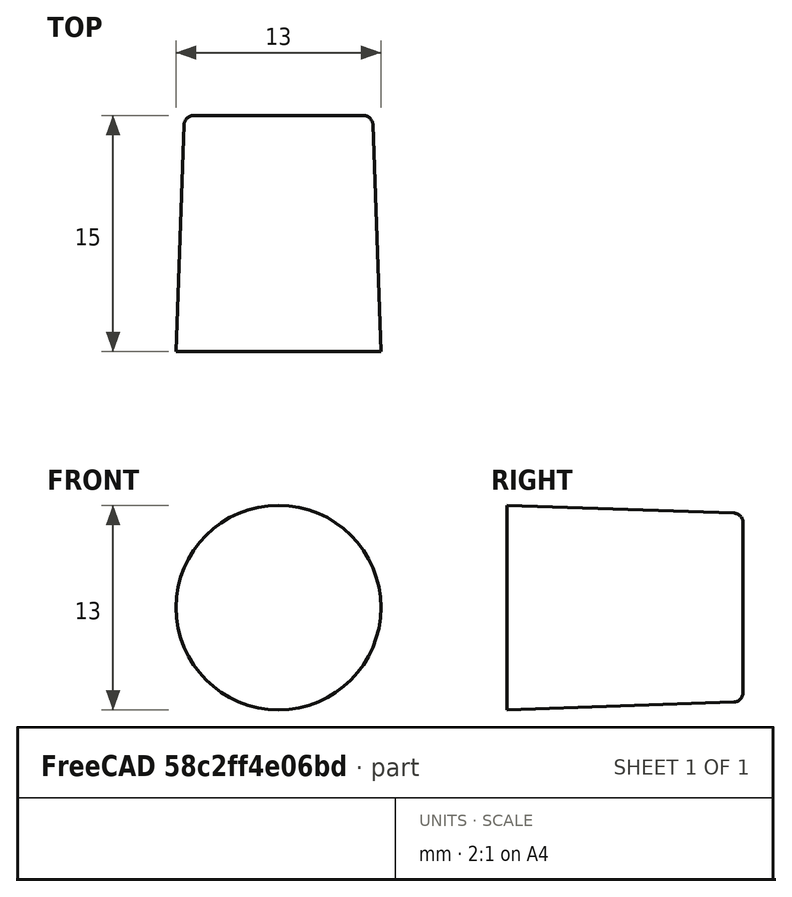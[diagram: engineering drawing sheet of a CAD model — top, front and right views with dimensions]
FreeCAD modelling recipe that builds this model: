
FCSTD DOCUMENT  (FreeCAD 0.18R15619 (Git))
Label: knob-rubber
License: All rights reserved
LicenseURL: http://en.wikipedia.org/wiki/All_rights_reserved
objects: Sketcher::SketchObject×1, PartDesign::Revolution×1, PartDesign::Body×1
note: 4 computed .brp shape members not serialized (recipe doc carries the construction recipe); baked Part::Feature solids carry a one-line shape summary decoded from their .brp

FEATURE [Sketcher::SketchObject] Sketch
  MapMode = 5
  Support = -> [XY_Plane]
  sketch-geometry (5):
    g0: LineSegment StartX=0 StartY=0 StartZ=0 EndX=0 EndY=15 EndZ=0
    g1: LineSegment StartX=0 StartY=15 StartZ=0 EndX=5.40036 EndY=15 EndZ=0
    g2: LineSegment StartX=6 StartY=14.4208 StartZ=0 EndX=6.5 EndY=0 EndZ=0
    g3: LineSegment StartX=6.5 StartY=0 StartZ=0 EndX=0 EndY=0 EndZ=0
    g4: ArcOfCircle CenterX=5.40036 CenterY=14.4 CenterZ=0 NormalX=0 NormalY=0 NormalZ=1 AngleXU=0 Radius=0.6 StartAngle=0.0346583 EndAngle=1.5708
  constraints (13):
    c: Coincident(g0,g1)
    c: Coincident(g2,g3)
    c: Coincident(g3,g0)
    c: Vertical(g0)
    c: Horizontal(g1)
    c: Horizontal(g3)
    c: Coincident(g0,g-1)
    c: Distance(g3) = 6.5
    c: Distance(g0) = 15
    c: Tangent(g1,g4) = 1.5708
    c: Tangent(g2,g4) = 1.5708
    c: Distance(g2,g0) = 6
    c: Radius(g4) = 0.6
FEATURE [PartDesign::Revolution] Revolution
  Angle = 360
  Axis = (0,1,0)
  Base = (0,0,0)
  Profile = -> Sketch
  ReferenceAxis = -> Sketch [V_Axis]
  Reversed = true
FEATURE [PartDesign::Body] Body
  Group = -> [Sketch,Revolution]
  Origin = -> Origin
  Tip = -> Revolution
